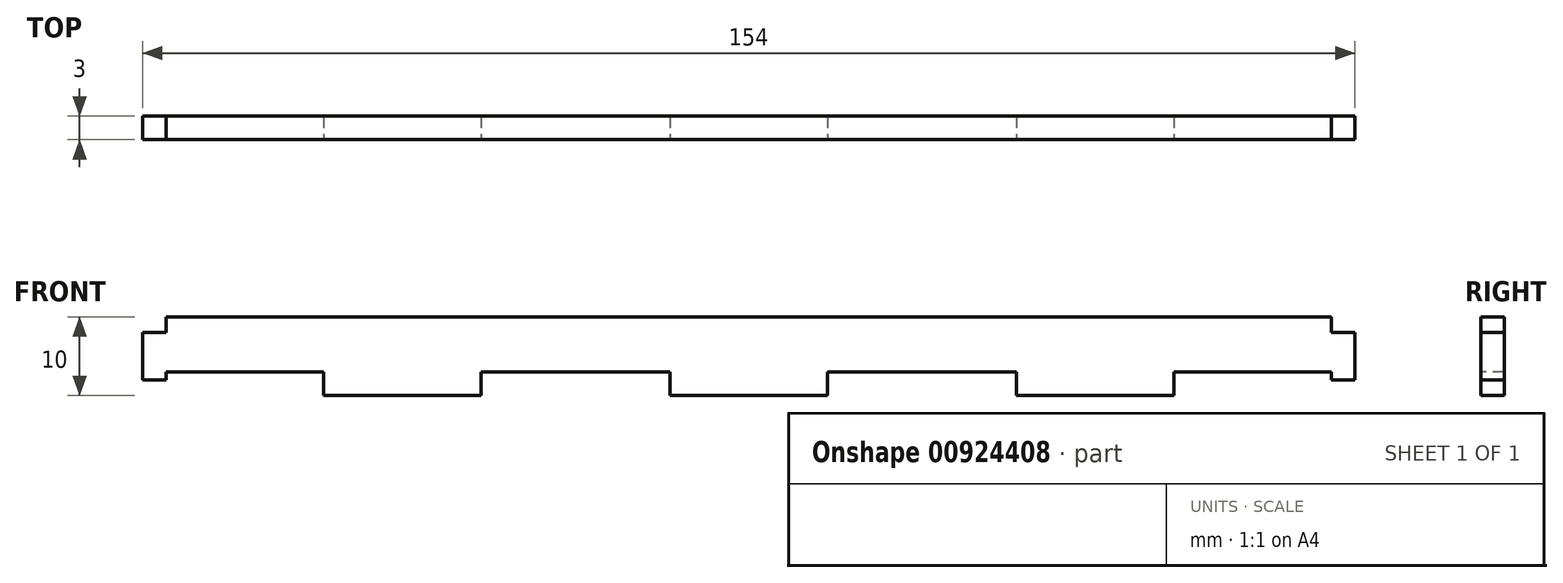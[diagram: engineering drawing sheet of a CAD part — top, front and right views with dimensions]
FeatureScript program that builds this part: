
annotation { "Feature Type Name" : "Feature", "Feature Type Description" : "" }
export const myFeature = defineFeature(function(context is Context, id is Id, definition is map)
    precondition{}
    {
        {
            var Q0;
            Q0=qCreatedBy(makeId("Front.planeOp"),FACE);
            var sketch = newSketch(context, id + "F0", { "sketchPlane" : qUnion([Q0])});
            skLineSegment(sketch, "E0.bottom", {"start": v(3, 0) * mm, "end": v(151, 0) * mm});
            skLineSegment(sketch, "E0.top", {"start": v(3, 10) * mm, "end": v(151, 10) * mm});
            skLineSegment(sketch, "E0.left", {"start": v(0, 2) * mm, "end": v(0, 8) * mm});
            skLineSegment(sketch, "E0.right", {"start": v(154, 2) * mm, "end": v(154, 8) * mm});
            skLineSegment(sketch, "E1", {"start": v(0, 8) * mm, "end": v(3, 8) * mm});
            skLineSegment(sketch, "E2", {"start": v(3, 8) * mm, "end": v(3, 10) * mm});
            skLineSegment(sketch, "E3", {"start": v(0, 2) * mm, "end": v(3, 2) * mm});
            skLineSegment(sketch, "E4", {"start": v(3, 2) * mm, "end": v(3, 0) * mm});
            skPoint(sketch, "E5", {"position": v(0, 4) * mm});
            skPoint(sketch, "E6.orphan", {"position": v(0, 0) * mm});
            skLineSegment(sketch, "E7", {"start": v(151, 10) * mm, "end": v(151, 8) * mm});
            skLineSegment(sketch, "E8", {"start": v(151, 8) * mm, "end": v(154, 8) * mm});
            skLineSegment(sketch, "E9", {"start": v(154, 2) * mm, "end": v(151, 2) * mm});
            skLineSegment(sketch, "E10", {"start": v(151, 2) * mm, "end": v(151, 0) * mm});
            skSolve(sketch);
        }
        {
            var Q0;
            Q0 = qSketchRegion(id + "F0", true);
            extrude(context, id + "F1", {"entities" : qUnion([Q0]), "depth" : 3 * mm, "offsetDistance" : 25 * mm});
        }
        {
            var Q0;
            Q0=makeQuery(id+"F1.opExtrude","CAP_FACE",FACE,{"disambiguationData":[OSD([sQuery(id+"F0.wireOp",EDGE,"E0.bottom"),sQuery(id+"F0.wireOp",EDGE,"E0.top"),sQuery(id+"F0.wireOp",EDGE,"E0.left"),sQuery(id+"F0.wireOp",EDGE,"E0.right"),sQuery(id+"F0.wireOp",EDGE,"E1"),sQuery(id+"F0.wireOp",EDGE,"E2"),sQuery(id+"F0.wireOp",EDGE,"E3"),sQuery(id+"F0.wireOp",EDGE,"E4"),sQuery(id+"F0.wireOp",EDGE,"E7"),sQuery(id+"F0.wireOp",EDGE,"E8"),sQuery(id+"F0.wireOp",EDGE,"E9"),sQuery(id+"F0.wireOp",EDGE,"E10")])],"isStart":false});
            var sketch = newSketch(context, id + "F2", { "sketchPlane" : qUnion([Q0])});
            skLineSegment(sketch, "E11", {"start": v(23, 1) * mm, "end": v(43, 1) * mm, "construction": true});
            skLineSegment(sketch, "E12", {"start": v(67, 1.14) * mm, "end": v(87, 1.14) * mm, "construction": true});
            skLineSegment(sketch, "E13", {"start": v(111, 1.14) * mm, "end": v(131, 1.14) * mm, "construction": true});
            skPoint(sketch, "E14.firstSnap0", {"position": v(3, 1) * mm});
            skLineSegment(sketch, "E14.bottom", {"start": v(3, 3) * mm, "end": v(23, 3) * mm});
            skLineSegment(sketch, "E14.top", {"start": v(3, 0) * mm, "end": v(23, 0) * mm});
            skLineSegment(sketch, "E14.left", {"start": v(3, 3) * mm, "end": v(3, 0) * mm});
            skLineSegment(sketch, "E14.right", {"start": v(23, 3) * mm, "end": v(23, 0) * mm});
            skLineSegment(sketch, "E15.bottom", {"start": v(43, 3) * mm, "end": v(67, 3) * mm});
            skLineSegment(sketch, "E15.top", {"start": v(43, 0) * mm, "end": v(67, 0) * mm});
            skLineSegment(sketch, "E15.left", {"start": v(43, 3) * mm, "end": v(43, 0) * mm});
            skLineSegment(sketch, "E15.right", {"start": v(67, 3) * mm, "end": v(67, 0) * mm});
            skLineSegment(sketch, "E16.bottom", {"start": v(87, 3) * mm, "end": v(111, 3) * mm});
            skLineSegment(sketch, "E16.top", {"start": v(87, 0) * mm, "end": v(111, 0) * mm});
            skLineSegment(sketch, "E16.left", {"start": v(87, 3) * mm, "end": v(87, 0) * mm});
            skLineSegment(sketch, "E16.right", {"start": v(111, 3) * mm, "end": v(111, 0) * mm});
            skLineSegment(sketch, "E17.bottom", {"start": v(151, 0) * mm, "end": v(131, 0) * mm});
            skLineSegment(sketch, "E17.top", {"start": v(151, 3) * mm, "end": v(131, 3) * mm});
            skLineSegment(sketch, "E17.left", {"start": v(151, 0) * mm, "end": v(151, 3) * mm});
            skLineSegment(sketch, "E17.right", {"start": v(131, 0) * mm, "end": v(131, 3) * mm});
            skSolve(sketch);
        }
        {
            var Q0;
            Q0 = qSketchRegion(id + "F2", true);
            extrude(context, id + "F3", {"entities" : qUnion([Q0]), "operationType" : NewBodyOperationType.REMOVE, "endBound" : BoundingType.THROUGH_ALL, "oppositeDirection" : true, "depth" : 25 * mm, "offsetDistance" : 25 * mm});
        }
    });
